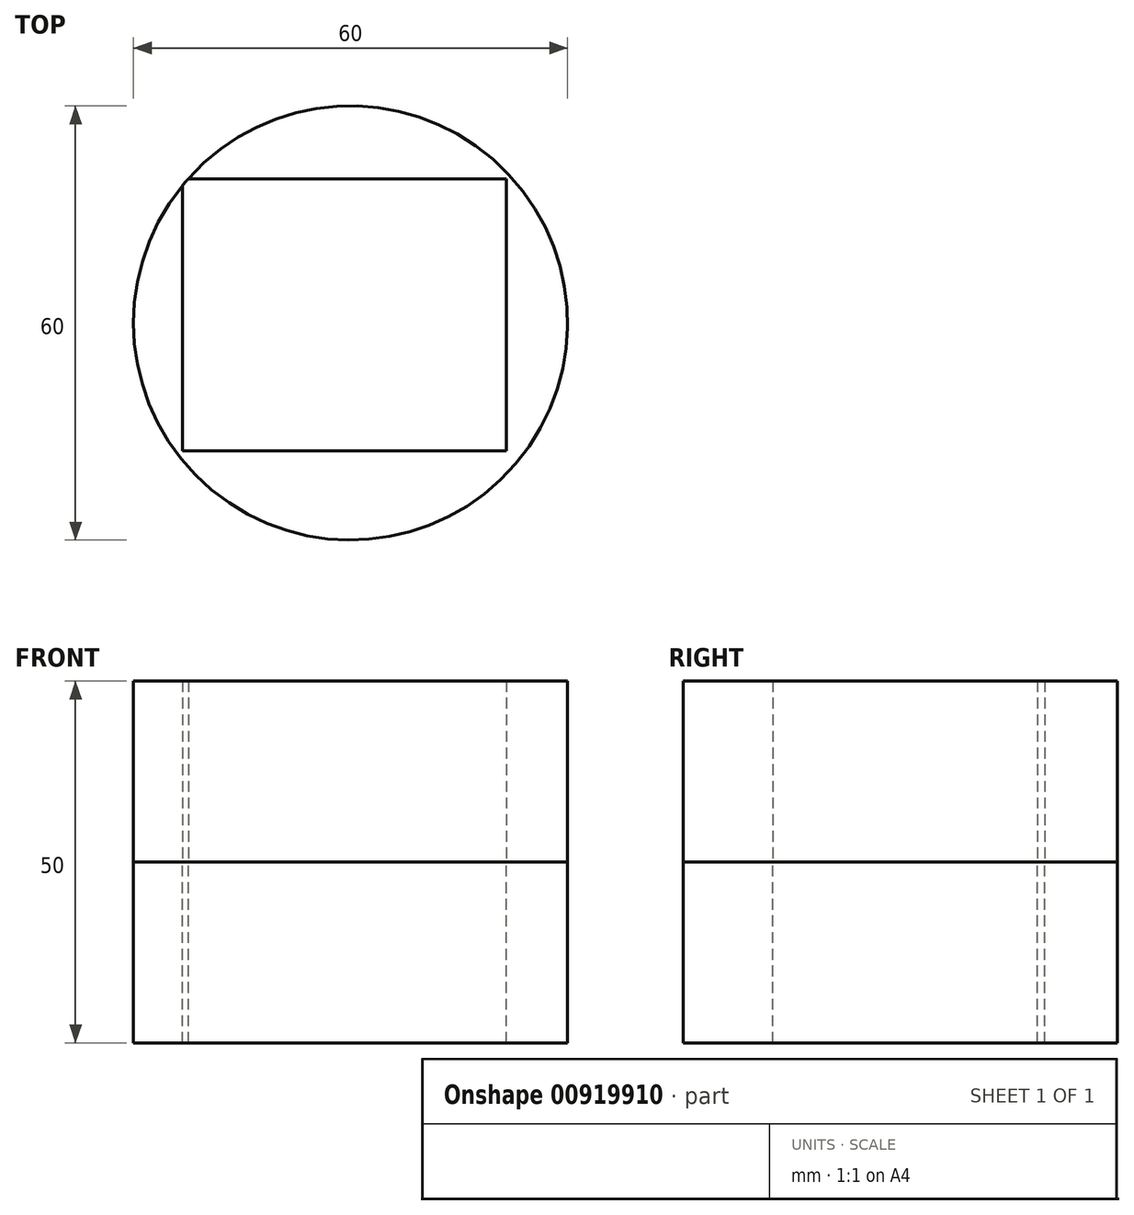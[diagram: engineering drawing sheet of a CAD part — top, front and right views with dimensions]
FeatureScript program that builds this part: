
annotation { "Feature Type Name" : "Feature", "Feature Type Description" : "" }
export const myFeature = defineFeature(function(context is Context, id is Id, definition is map)
    precondition{}
    {
        {
            var Q0;
            Q0=qCreatedBy(makeId("Top.planeOp"),FACE);
            var sketch = newSketch(context, id + "F0", { "sketchPlane" : qUnion([Q0])});
            skCircle(sketch, "E0", {"center": v(0, 0) * mm, "radius": 30 * mm});
            skSolve(sketch);
        }
        {
            var Q0;
            Q0=makeQuery(id+"F0.imprint","IMPRINT",FACE,{"disambiguationData":[TD([[makeQuery(id+"F0.imprint","IMPRINT",EDGE,{"derivedFrom":sQuery(id+"F0.wireOp",EDGE,"E0")}),1.0]])]});
            var sketch = newSketch(context, id + "F1", { "sketchPlane" : qUnion([Q0])});
            skLineSegment(sketch, "E1.bottom", {"start": v(-23.25, 19.94) * mm, "end": v(21.51, 19.94) * mm});
            skLineSegment(sketch, "E1.top", {"start": v(-23.25, -17.65) * mm, "end": v(21.51, -17.65) * mm});
            skLineSegment(sketch, "E1.left", {"start": v(-23.25, 19.94) * mm, "end": v(-23.25, -17.65) * mm});
            skLineSegment(sketch, "E1.right", {"start": v(21.51, 19.94) * mm, "end": v(21.51, -17.65) * mm});
            skSolve(sketch);
        }
        {
            var Q0;
            Q0=makeQuery(id+"F0.imprint","IMPRINT",FACE,{"disambiguationData":[TD([[makeQuery(id+"F0.imprint","IMPRINT",EDGE,{"derivedFrom":sQuery(id+"F0.wireOp",EDGE,"E0")}),1.0]])]});
            var Q1;
            {var subQ2=sQuery(id+"F1.wireOp",EDGE,"E1.top");Q1=makeQuery(id+"F1.imprint","IMPRINT",FACE,{"disambiguationData":[TD([[makeQuery(id+"F1.imprint","IMPRINT",EDGE,{"derivedFrom":subQ2}),-1.0]])]});}
            extrude(context, id + "F2", {"entities" : qUnion([Q0, Q1]), "depth" : -25 * mm, "offsetDistance" : 25 * mm});
        }
        {
            var Q0;
            Q0=makeQuery(id+"F2.opExtrude","CAP_FACE",FACE,{"disambiguationData":[OSD([sQuery(id+"F0.wireOp",EDGE,"E0"),sQuery(id+"F1.wireOp",EDGE,"E1.bottom"),sQuery(id+"F1.wireOp",EDGE,"E1.top"),sQuery(id+"F1.wireOp",EDGE,"E1.left"),sQuery(id+"F1.wireOp",EDGE,"E1.right")])],"isStart":true});
            extrude(context, id + "F3", {"entities" : qUnion([Q0]), "depth" : 25 * mm, "offsetDistance" : 25 * mm});
        }
    });
